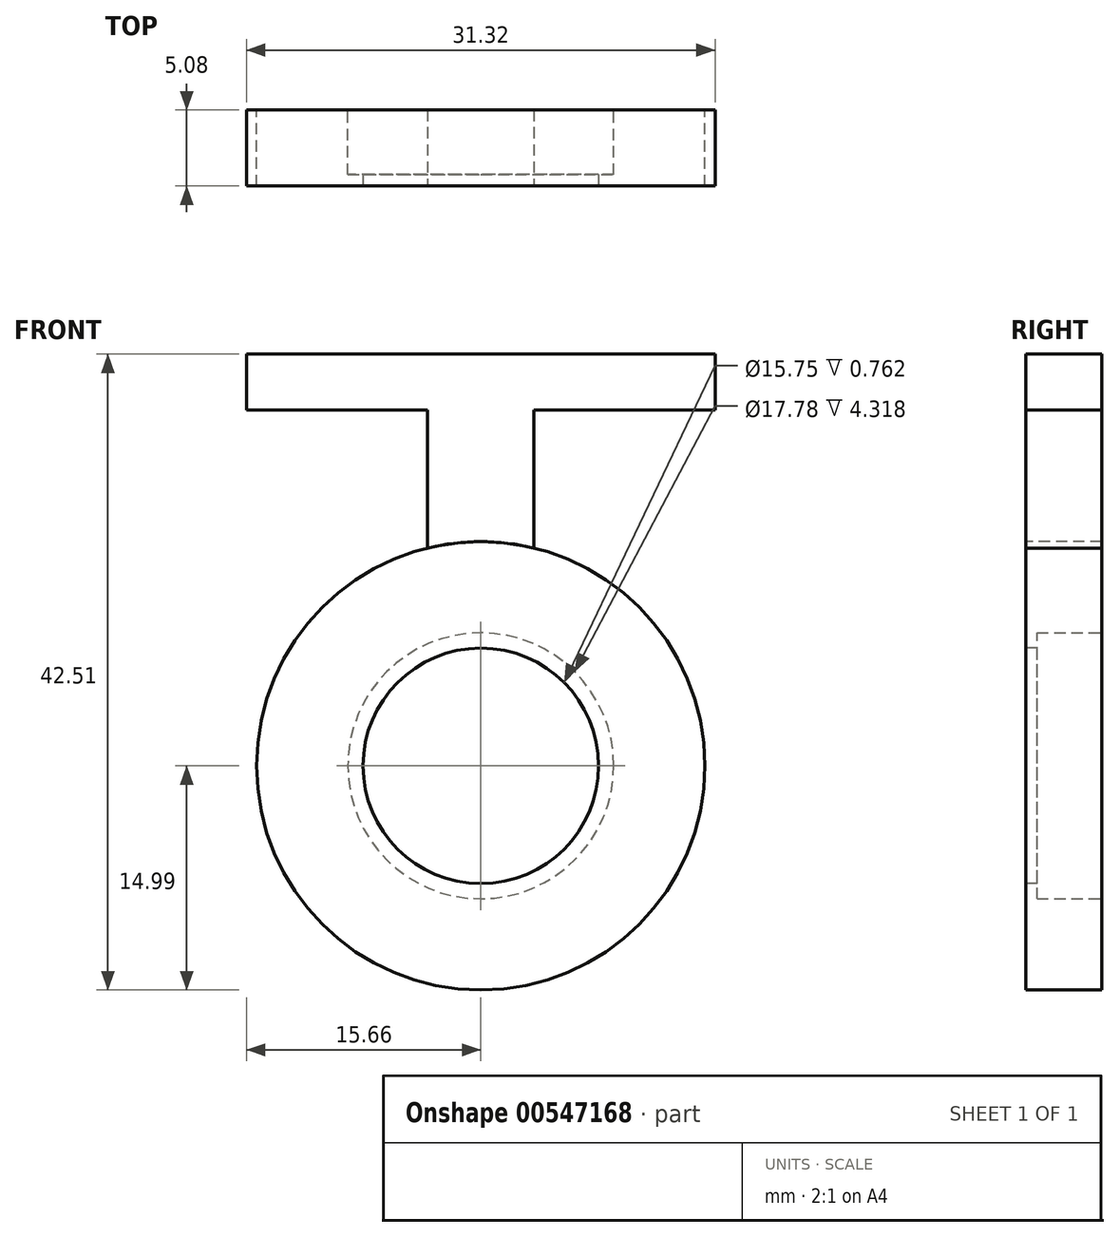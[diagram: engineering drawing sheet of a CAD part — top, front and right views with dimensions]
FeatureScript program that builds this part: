
annotation { "Feature Type Name" : "Feature", "Feature Type Description" : "" }
export const myFeature = defineFeature(function(context is Context, id is Id, definition is map)
    precondition{}
    {
        {
            var Q0;
            Q0=qCreatedBy(makeId("Front.planeOp"),FACE);
            var sketch = newSketch(context, id + "F0", { "sketchPlane" : qUnion([Q0])});
            skCircle(sketch, "E0", {"center": v(0, 0) * mm, "radius": 14.99 * mm});
            skSolve(sketch);
        }
        {
            var Q0;
            Q0 = qSketchRegion(id + "F0", true);
            var Q1;
            Q1=makeQuery(id+"F0.imprint","IMPRINT",FACE,{"disambiguationData":[TD([[makeQuery(id+"F0.imprint","IMPRINT",EDGE,{"derivedFrom":sQuery(id+"F0.wireOp",EDGE,"E0")}),1.0]])]});
            extrude(context, id + "F1", {"entities" : qUnion([Q0, Q1]), "depth" : 5.08 * mm, "offsetDistance" : 25.4 * mm});
        }
        {
            var Q0;
            Q0=makeQuery(id+"F1.opExtrude","CAP_FACE",FACE,{"disambiguationData":[OSD([sQuery(id+"F0.wireOp",EDGE,"E0")])],"isStart":false});
            var sketch = newSketch(context, id + "F2", { "sketchPlane" : qUnion([Q0])});
            skCircle(sketch, "E1", {"center": v(0, 0) * mm, "radius": 7.87 * mm});
            skSolve(sketch);
        }
        {
            var Q0;
            Q0=makeQuery(id+"F2.imprint","IMPRINT",FACE,{"disambiguationData":[TD([[makeQuery(id+"F2.imprint","IMPRINT",EDGE,{"derivedFrom":sQuery(id+"F2.wireOp",EDGE,"E1")}),1.0]])]});
            extrude(context, id + "F3", {"entities" : qUnion([Q0]), "operationType" : NewBodyOperationType.REMOVE, "endBound" : BoundingType.THROUGH_ALL, "oppositeDirection" : true, "depth" : 2.5 * mm, "offsetDistance" : 25.4 * mm});
        }
        {
            var Q0;
            Q0=qCreatedBy(makeId("Front.planeOp"),FACE);
            var sketch = newSketch(context, id + "F4", { "sketchPlane" : qUnion([Q0])});
            skCircle(sketch, "E2", {"center": v(0, 0) * mm, "radius": 8.9 * mm});
            skSolve(sketch);
        }
        {
            var Q0;
            Q0=makeQuery(id+"F4.imprint","IMPRINT",FACE,{"disambiguationData":[TD([[makeQuery(id+"F4.imprint","IMPRINT",EDGE,{"derivedFrom":sQuery(id+"F4.wireOp",EDGE,"E2")}),1.0]])]});
            extrude(context, id + "F5", {"entities" : qUnion([Q0]), "operationType" : NewBodyOperationType.REMOVE, "depth" : 4.32 * mm, "offsetDistance" : 25.4 * mm});
        }
        {
            var Q0;
            Q0=makeQuery(id+"F2.imprint","IMPRINT",FACE,{"disambiguationData":[TD([[makeQuery(id+"F2.imprint","IMPRINT",EDGE,{"derivedFrom":sQuery(id+"F2.wireOp",EDGE,"E1")}),-1.0]])]});
            var sketch = newSketch(context, id + "F6", { "sketchPlane" : qUnion([Q0])});
            skLineSegment(sketch, "E3.bottom", {"start": v(3.56, 14.03) * mm, "end": v(-3.56, 14.03) * mm});
            skLineSegment(sketch, "E3.top", {"start": v(3.56, 24.19) * mm, "end": v(-3.56, 24.19) * mm});
            skLineSegment(sketch, "E3.left", {"start": v(3.56, 14.03) * mm, "end": v(3.56, 24.19) * mm});
            skLineSegment(sketch, "E3.right", {"start": v(-3.56, 14.03) * mm, "end": v(-3.56, 24.19) * mm});
            skPoint(sketch, "E3.middle", {"position": v(0, 19.1) * mm});
            skSolve(sketch);
        }
        {
            var Q0;
            {var subQ0=sQuery(id+"F6.wireOp",EDGE,"E3.top");Q0=makeQuery(id+"F6.imprint","IMPRINT",FACE,{"disambiguationData":[TD([[makeQuery(id+"F6.imprint","IMPRINT",EDGE,{"derivedFrom":subQ0}),1.0]])]});}
            extrude(context, id + "F7", {"entities" : qUnion([Q0]), "oppositeDirection" : true, "depth" : 5.08 * mm, "offsetDistance" : 25.4 * mm});
        }
        {
            var Q0;
            Q0=makeQuery(id+"F7.opExtrude","CAP_FACE",FACE,{"disambiguationData":[OSD([sQuery(id+"F0.wireOp",EDGE,"E0"),sQuery(id+"F6.wireOp",EDGE,"E3.top"),sQuery(id+"F6.wireOp",EDGE,"E3.left"),sQuery(id+"F6.wireOp",EDGE,"E3.right")])],"isStart":true});
            var sketch = newSketch(context, id + "F8", { "sketchPlane" : qUnion([Q0])});
            skLineSegment(sketch, "E4.bottom", {"start": v(15.66, 27.52) * mm, "end": v(-15.66, 27.52) * mm});
            skLineSegment(sketch, "E4.top", {"start": v(15.66, 23.8) * mm, "end": v(-15.66, 23.8) * mm});
            skLineSegment(sketch, "E4.left", {"start": v(15.66, 27.52) * mm, "end": v(15.66, 23.8) * mm});
            skLineSegment(sketch, "E4.right", {"start": v(-15.66, 27.52) * mm, "end": v(-15.66, 23.8) * mm});
            skPoint(sketch, "E4.middle", {"position": v(0, 25.66) * mm});
            skSolve(sketch);
        }
        {
            var Q0;
            Q0 = qSketchRegion(id + "F8", true);
            extrude(context, id + "F9", {"entities" : qUnion([Q0]), "operationType" : NewBodyOperationType.ADD, "oppositeDirection" : true, "depth" : 5.08 * mm, "offsetDistance" : 25.4 * mm});
        }
    });
